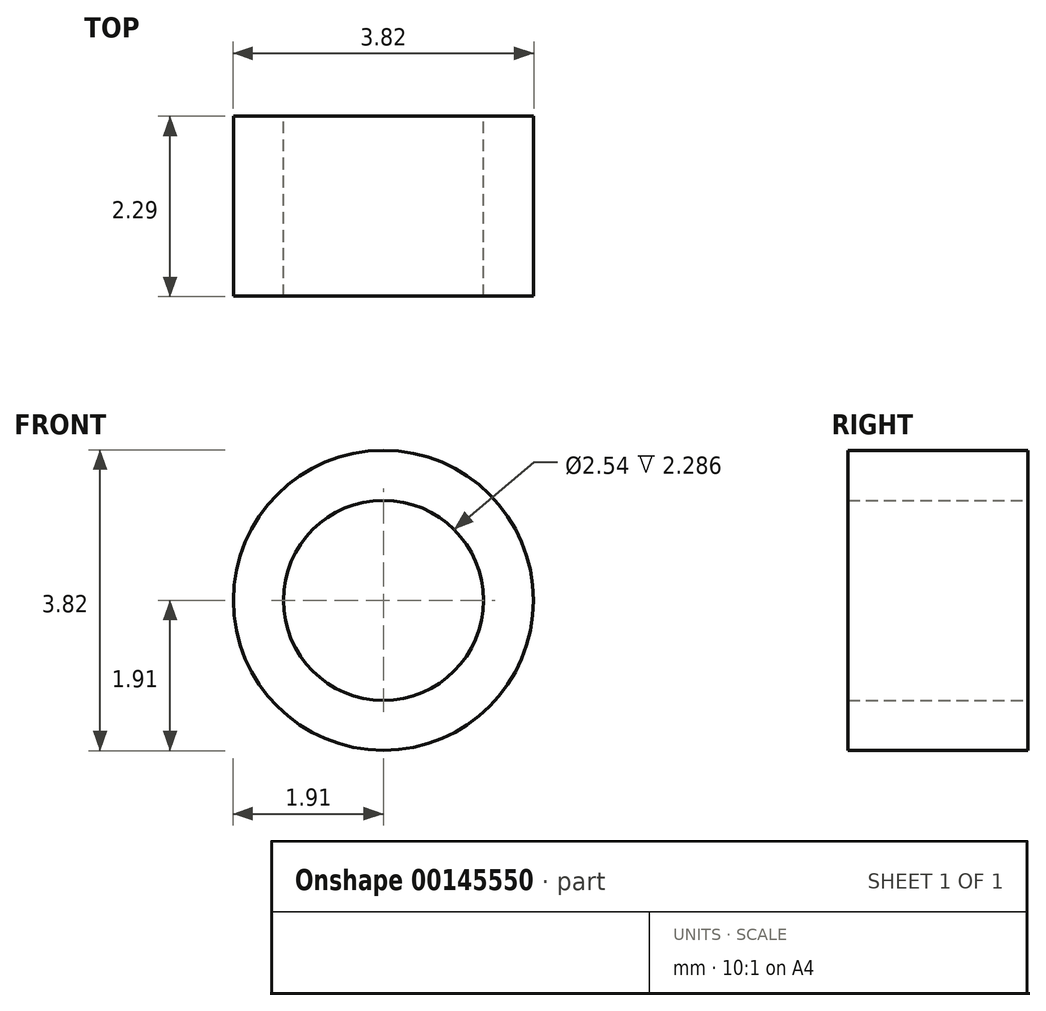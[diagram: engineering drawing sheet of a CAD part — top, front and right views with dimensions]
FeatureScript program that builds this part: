
annotation { "Feature Type Name" : "Feature", "Feature Type Description" : "" }
export const myFeature = defineFeature(function(context is Context, id is Id, definition is map)
    precondition{}
    {
        {
            var Q0;
            Q0=qCreatedBy(makeId("Front.planeOp"),FACE);
            var sketch = newSketch(context, id + "F0", { "sketchPlane" : qUnion([Q0])});
            skCircle(sketch, "E0", {"center": v(0, 0) * mm, "radius": 1.27 * mm});
            skCircle(sketch, "E1", {"center": v(0, 0) * mm, "radius": 1.9 * mm});
            skSolve(sketch);
        }
        {
            var Q0;
            Q0 = qSketchRegion(id + "F0", true);
            extrude(context, id + "F1", {"entities" : qUnion([Q0]), "depth" : 2.3 * mm});
        }
    });
